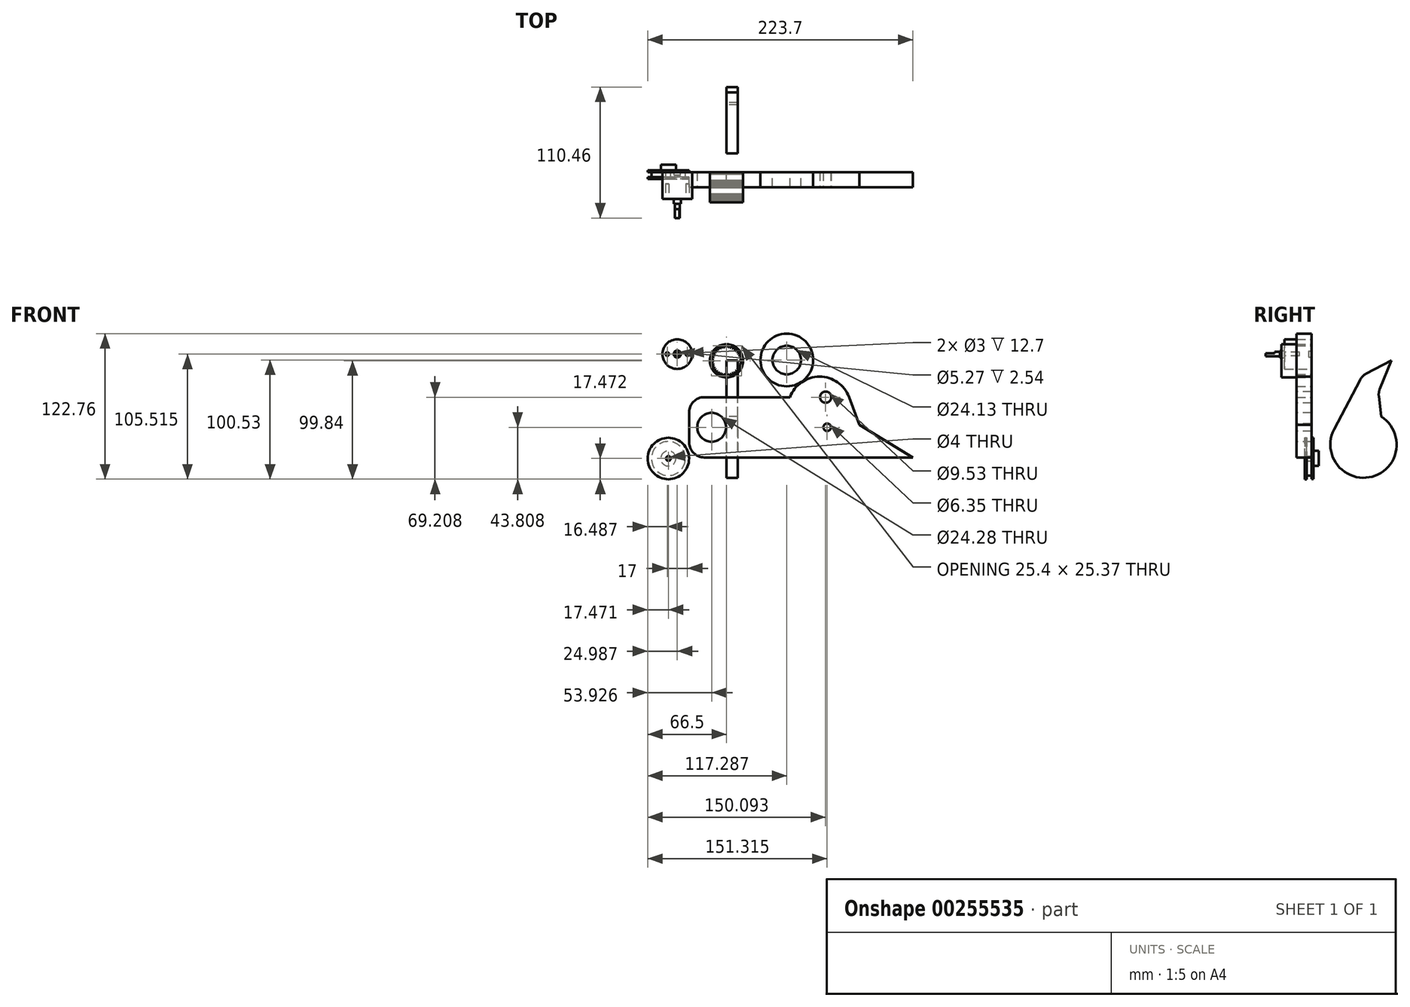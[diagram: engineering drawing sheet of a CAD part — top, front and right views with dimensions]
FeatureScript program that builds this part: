
annotation { "Feature Type Name" : "Feature", "Feature Type Description" : "" }
export const myFeature = defineFeature(function(context is Context, id is Id, definition is map)
    precondition{}
    {
        {
            var Q0;
            Q0=qCreatedBy(makeId("Front.planeOp"),FACE);
            var sketch = newSketch(context, id + "F0", { "sketchPlane" : qUnion([Q0])});
            skCircle(sketch, "E0", {"center": v(0, 41.16) * mm, "radius": 12.7 * mm});
            skLineSegment(sketch, "E1", {"start": v(-0.59, 28.47) * mm, "end": v(-0.26, 29.62) * mm});
            skLineSegment(sketch, "E2", {"start": v(-0.26, 29.62) * mm, "end": v(0, 29.62) * mm});
            skLineSegment(sketch, "E3", {"start": v(0, 28.46) * mm, "end": v(0, 28.58) * mm});
            skLineSegment(sketch, "E4.MirrorCS", {"start": v(0.59, 28.47) * mm, "end": v(0.26, 29.62) * mm});
            skLineSegment(sketch, "E5.MirrorCS", {"start": v(0.26, 29.62) * mm, "end": v(0, 29.62) * mm});
            skLineSegment(sketch, "E6.1.0", {"start": v(2.47, 28.7) * mm, "end": v(1.98, 29.78) * mm});
            skLineSegment(sketch, "E6.1.1", {"start": v(1.3, 28.53) * mm, "end": v(1.46, 29.7) * mm});
            skLineSegment(sketch, "E6.1.2", {"start": v(1.9, 28.6) * mm, "end": v(1.88, 28.72) * mm});
            skLineSegment(sketch, "E6.1.3", {"start": v(1.98, 29.78) * mm, "end": v(1.72, 29.75) * mm});
            skLineSegment(sketch, "E6.1.4", {"start": v(1.46, 29.7) * mm, "end": v(1.72, 29.75) * mm});
            skLineSegment(sketch, "E6.2.0", {"start": v(4.3, 29.21) * mm, "end": v(3.66, 30.2) * mm});
            skLineSegment(sketch, "E6.2.1", {"start": v(3.18, 28.86) * mm, "end": v(3.15, 30.05) * mm});
            skLineSegment(sketch, "E6.2.2", {"start": v(3.74, 29.02) * mm, "end": v(3.7, 29.13) * mm});
            skLineSegment(sketch, "E6.2.3", {"start": v(3.66, 30.2) * mm, "end": v(3.4, 30.13) * mm});
            skLineSegment(sketch, "E6.2.4", {"start": v(3.15, 30.05) * mm, "end": v(3.4, 30.13) * mm});
            skLineSegment(sketch, "E6.3.0", {"start": v(6.03, 29.99) * mm, "end": v(5.25, 30.87) * mm});
            skLineSegment(sketch, "E6.3.1", {"start": v(4.97, 29.48) * mm, "end": v(4.77, 30.64) * mm});
            skLineSegment(sketch, "E6.3.2", {"start": v(5.51, 29.72) * mm, "end": v(5.46, 29.82) * mm});
            skLineSegment(sketch, "E6.3.3", {"start": v(5.25, 30.87) * mm, "end": v(5, 30.76) * mm});
            skLineSegment(sketch, "E6.3.4", {"start": v(4.77, 30.64) * mm, "end": v(5, 30.76) * mm});
            skLineSegment(sketch, "E6.4.0", {"start": v(7.63, 31) * mm, "end": v(6.72, 31.77) * mm});
            skLineSegment(sketch, "E6.4.1", {"start": v(6.66, 30.35) * mm, "end": v(6.28, 31.47) * mm});
            skLineSegment(sketch, "E6.4.2", {"start": v(7.15, 30.67) * mm, "end": v(7.09, 30.76) * mm});
            skLineSegment(sketch, "E6.4.3", {"start": v(6.72, 31.77) * mm, "end": v(6.5, 31.62) * mm});
            skLineSegment(sketch, "E6.4.4", {"start": v(6.28, 31.47) * mm, "end": v(6.5, 31.62) * mm});
            skLineSegment(sketch, "E6.5.0", {"start": v(9.06, 32.26) * mm, "end": v(8.05, 32.88) * mm});
            skLineSegment(sketch, "E6.5.1", {"start": v(8.2, 31.46) * mm, "end": v(7.66, 32.52) * mm});
            skLineSegment(sketch, "E6.5.2", {"start": v(8.64, 31.85) * mm, "end": v(8.56, 31.93) * mm});
            skLineSegment(sketch, "E6.5.3", {"start": v(8.05, 32.88) * mm, "end": v(7.85, 32.7) * mm});
            skLineSegment(sketch, "E6.5.4", {"start": v(7.66, 32.52) * mm, "end": v(7.85, 32.7) * mm});
            skLineSegment(sketch, "E6.6.0", {"start": v(10.29, 33.71) * mm, "end": v(9.2, 34.17) * mm});
            skLineSegment(sketch, "E6.6.1", {"start": v(9.55, 32.8) * mm, "end": v(8.86, 33.76) * mm});
            skLineSegment(sketch, "E6.6.2", {"start": v(9.93, 33.24) * mm, "end": v(9.84, 33.31) * mm});
            skLineSegment(sketch, "E6.6.3", {"start": v(9.2, 34.17) * mm, "end": v(9.03, 33.96) * mm});
            skLineSegment(sketch, "E6.6.4", {"start": v(8.86, 33.76) * mm, "end": v(9.03, 33.96) * mm});
            skLineSegment(sketch, "E6.7.0", {"start": v(11.28, 35.33) * mm, "end": v(10.13, 35.62) * mm});
            skLineSegment(sketch, "E6.7.1", {"start": v(10.7, 34.3) * mm, "end": v(9.87, 35.16) * mm});
            skLineSegment(sketch, "E6.7.2", {"start": v(11, 34.81) * mm, "end": v(10.9, 34.87) * mm});
            skLineSegment(sketch, "E6.7.3", {"start": v(10.13, 35.62) * mm, "end": v(10, 35.39) * mm});
            skLineSegment(sketch, "E6.7.4", {"start": v(9.87, 35.16) * mm, "end": v(10, 35.39) * mm});
            skLineSegment(sketch, "E6.8.0", {"start": v(12.02, 37.07) * mm, "end": v(10.84, 37.19) * mm});
            skLineSegment(sketch, "E6.8.1", {"start": v(11.6, 35.98) * mm, "end": v(10.65, 36.7) * mm});
            skLineSegment(sketch, "E6.8.2", {"start": v(11.82, 36.52) * mm, "end": v(11.72, 36.56) * mm});
            skLineSegment(sketch, "E6.8.3", {"start": v(10.84, 37.19) * mm, "end": v(10.75, 36.94) * mm});
            skLineSegment(sketch, "E6.8.4", {"start": v(10.65, 36.7) * mm, "end": v(10.75, 36.94) * mm});
            skLineSegment(sketch, "E6.9.0", {"start": v(12.5, 38.91) * mm, "end": v(11.31, 38.85) * mm});
            skLineSegment(sketch, "E6.9.1", {"start": v(12.24, 37.76) * mm, "end": v(11.2, 38.33) * mm});
            skLineSegment(sketch, "E6.9.2", {"start": v(12.38, 38.33) * mm, "end": v(12.27, 38.36) * mm});
            skLineSegment(sketch, "E6.9.3", {"start": v(11.31, 38.85) * mm, "end": v(11.25, 38.6) * mm});
            skLineSegment(sketch, "E6.9.4", {"start": v(11.2, 38.33) * mm, "end": v(11.25, 38.6) * mm});
            skLineSegment(sketch, "E6.10.0", {"start": v(12.7, 40.8) * mm, "end": v(11.53, 40.56) * mm});
            skLineSegment(sketch, "E6.10.1", {"start": v(12.6, 39.63) * mm, "end": v(11.5, 40.03) * mm});
            skLineSegment(sketch, "E6.10.2", {"start": v(12.66, 40.21) * mm, "end": v(12.55, 40.22) * mm});
            skLineSegment(sketch, "E6.10.3", {"start": v(11.53, 40.56) * mm, "end": v(11.51, 40.3) * mm});
            skLineSegment(sketch, "E6.10.4", {"start": v(11.5, 40.03) * mm, "end": v(11.51, 40.3) * mm});
            skLineSegment(sketch, "E6.11.0", {"start": v(12.6, 42.7) * mm, "end": v(11.5, 42.29) * mm});
            skLineSegment(sketch, "E6.11.1", {"start": v(12.7, 41.52) * mm, "end": v(11.53, 41.76) * mm});
            skLineSegment(sketch, "E6.11.2", {"start": v(12.66, 42.1) * mm, "end": v(12.55, 42.1) * mm});
            skLineSegment(sketch, "E6.11.3", {"start": v(11.5, 42.29) * mm, "end": v(11.51, 42.02) * mm});
            skLineSegment(sketch, "E6.11.4", {"start": v(11.53, 41.76) * mm, "end": v(11.51, 42.02) * mm});
            skLineSegment(sketch, "E6.12.0", {"start": v(12.24, 44.56) * mm, "end": v(11.2, 43.99) * mm});
            skLineSegment(sketch, "E6.12.1", {"start": v(12.5, 43.41) * mm, "end": v(11.31, 43.47) * mm});
            skLineSegment(sketch, "E6.12.2", {"start": v(12.38, 43.99) * mm, "end": v(12.27, 43.96) * mm});
            skLineSegment(sketch, "E6.12.3", {"start": v(11.2, 43.99) * mm, "end": v(11.25, 43.73) * mm});
            skLineSegment(sketch, "E6.12.4", {"start": v(11.31, 43.47) * mm, "end": v(11.25, 43.73) * mm});
            skLineSegment(sketch, "E6.13.0", {"start": v(11.6, 46.34) * mm, "end": v(10.65, 45.62) * mm});
            skLineSegment(sketch, "E6.13.1", {"start": v(12.02, 45.25) * mm, "end": v(10.84, 45.13) * mm});
            skLineSegment(sketch, "E6.13.2", {"start": v(11.82, 45.8) * mm, "end": v(11.72, 45.76) * mm});
            skLineSegment(sketch, "E6.13.3", {"start": v(10.65, 45.62) * mm, "end": v(10.75, 45.38) * mm});
            skLineSegment(sketch, "E6.13.4", {"start": v(10.84, 45.13) * mm, "end": v(10.75, 45.38) * mm});
            skLineSegment(sketch, "E6.14.0", {"start": v(10.7, 48.01) * mm, "end": v(9.87, 47.16) * mm});
            skLineSegment(sketch, "E6.14.1", {"start": v(11.28, 47) * mm, "end": v(10.13, 46.7) * mm});
            skLineSegment(sketch, "E6.14.2", {"start": v(11, 47.51) * mm, "end": v(10.9, 47.45) * mm});
            skLineSegment(sketch, "E6.14.3", {"start": v(9.87, 47.16) * mm, "end": v(10, 46.93) * mm});
            skLineSegment(sketch, "E6.14.4", {"start": v(10.13, 46.7) * mm, "end": v(10, 46.93) * mm});
            skLineSegment(sketch, "E6.15.0", {"start": v(9.55, 49.53) * mm, "end": v(8.86, 48.56) * mm});
            skLineSegment(sketch, "E6.15.1", {"start": v(10.29, 48.61) * mm, "end": v(9.2, 48.15) * mm});
            skLineSegment(sketch, "E6.15.2", {"start": v(9.93, 49.08) * mm, "end": v(9.84, 49) * mm});
            skLineSegment(sketch, "E6.15.3", {"start": v(8.86, 48.56) * mm, "end": v(9.03, 48.36) * mm});
            skLineSegment(sketch, "E6.15.4", {"start": v(9.2, 48.15) * mm, "end": v(9.03, 48.36) * mm});
            skLineSegment(sketch, "E6.16.0", {"start": v(8.2, 50.86) * mm, "end": v(7.66, 49.8) * mm});
            skLineSegment(sketch, "E6.16.1", {"start": v(9.06, 50.06) * mm, "end": v(8.05, 49.44) * mm});
            skLineSegment(sketch, "E6.16.2", {"start": v(8.64, 50.47) * mm, "end": v(8.56, 50.39) * mm});
            skLineSegment(sketch, "E6.16.3", {"start": v(7.66, 49.8) * mm, "end": v(7.85, 49.62) * mm});
            skLineSegment(sketch, "E6.16.4", {"start": v(8.05, 49.44) * mm, "end": v(7.85, 49.62) * mm});
            skLineSegment(sketch, "E6.17.0", {"start": v(6.66, 51.97) * mm, "end": v(6.28, 50.85) * mm});
            skLineSegment(sketch, "E6.17.1", {"start": v(7.63, 51.31) * mm, "end": v(6.72, 50.55) * mm});
            skLineSegment(sketch, "E6.17.2", {"start": v(7.15, 51.65) * mm, "end": v(7.09, 51.56) * mm});
            skLineSegment(sketch, "E6.17.3", {"start": v(6.28, 50.85) * mm, "end": v(6.5, 50.7) * mm});
            skLineSegment(sketch, "E6.17.4", {"start": v(6.72, 50.55) * mm, "end": v(6.5, 50.7) * mm});
            skLineSegment(sketch, "E6.18.0", {"start": v(4.97, 52.85) * mm, "end": v(4.77, 51.68) * mm});
            skLineSegment(sketch, "E6.18.1", {"start": v(6.03, 52.34) * mm, "end": v(5.25, 51.45) * mm});
            skLineSegment(sketch, "E6.18.2", {"start": v(5.51, 52.6) * mm, "end": v(5.46, 52.5) * mm});
            skLineSegment(sketch, "E6.18.3", {"start": v(4.77, 51.68) * mm, "end": v(5, 51.56) * mm});
            skLineSegment(sketch, "E6.18.4", {"start": v(5.25, 51.45) * mm, "end": v(5, 51.56) * mm});
            skLineSegment(sketch, "E6.19.0", {"start": v(3.18, 53.46) * mm, "end": v(3.15, 52.27) * mm});
            skLineSegment(sketch, "E6.19.1", {"start": v(4.3, 53.1) * mm, "end": v(3.66, 52.11) * mm});
            skLineSegment(sketch, "E6.19.2", {"start": v(3.74, 53.3) * mm, "end": v(3.7, 53.19) * mm});
            skLineSegment(sketch, "E6.19.3", {"start": v(3.15, 52.27) * mm, "end": v(3.4, 52.2) * mm});
            skLineSegment(sketch, "E6.19.4", {"start": v(3.66, 52.11) * mm, "end": v(3.4, 52.2) * mm});
            skLineSegment(sketch, "E6.20.0", {"start": v(1.3, 53.8) * mm, "end": v(1.46, 52.62) * mm});
            skLineSegment(sketch, "E6.20.1", {"start": v(2.47, 53.62) * mm, "end": v(1.98, 52.54) * mm});
            skLineSegment(sketch, "E6.20.2", {"start": v(1.9, 53.72) * mm, "end": v(1.88, 53.6) * mm});
            skLineSegment(sketch, "E6.20.3", {"start": v(1.46, 52.62) * mm, "end": v(1.72, 52.58) * mm});
            skLineSegment(sketch, "E6.20.4", {"start": v(1.98, 52.54) * mm, "end": v(1.72, 52.58) * mm});
            skLineSegment(sketch, "E6.21.0", {"start": v(-0.59, 53.85) * mm, "end": v(-0.26, 52.7) * mm});
            skLineSegment(sketch, "E6.21.1", {"start": v(0.59, 53.85) * mm, "end": v(0.26, 52.7) * mm});
            skLineSegment(sketch, "E6.21.2", {"start": v(0, 53.86) * mm, "end": v(0, 53.75) * mm});
            skLineSegment(sketch, "E6.21.3", {"start": v(-0.26, 52.7) * mm, "end": v(0, 52.7) * mm});
            skLineSegment(sketch, "E6.21.4", {"start": v(0.26, 52.7) * mm, "end": v(0, 52.7) * mm});
            skLineSegment(sketch, "E6.22.0", {"start": v(-2.47, 53.62) * mm, "end": v(-1.98, 52.54) * mm});
            skLineSegment(sketch, "E6.22.1", {"start": v(-1.3, 53.8) * mm, "end": v(-1.46, 52.62) * mm});
            skLineSegment(sketch, "E6.22.2", {"start": v(-1.9, 53.72) * mm, "end": v(-1.88, 53.6) * mm});
            skLineSegment(sketch, "E6.22.3", {"start": v(-1.98, 52.54) * mm, "end": v(-1.72, 52.58) * mm});
            skLineSegment(sketch, "E6.22.4", {"start": v(-1.46, 52.62) * mm, "end": v(-1.72, 52.58) * mm});
            skLineSegment(sketch, "E6.23.0", {"start": v(-4.3, 53.1) * mm, "end": v(-3.66, 52.11) * mm});
            skLineSegment(sketch, "E6.23.1", {"start": v(-3.18, 53.46) * mm, "end": v(-3.15, 52.27) * mm});
            skLineSegment(sketch, "E6.23.2", {"start": v(-3.74, 53.3) * mm, "end": v(-3.7, 53.19) * mm});
            skLineSegment(sketch, "E6.23.3", {"start": v(-3.66, 52.11) * mm, "end": v(-3.4, 52.2) * mm});
            skLineSegment(sketch, "E6.23.4", {"start": v(-3.15, 52.27) * mm, "end": v(-3.4, 52.2) * mm});
            skLineSegment(sketch, "E6.24.0", {"start": v(-6.03, 52.34) * mm, "end": v(-5.25, 51.45) * mm});
            skLineSegment(sketch, "E6.24.1", {"start": v(-4.97, 52.85) * mm, "end": v(-4.77, 51.68) * mm});
            skLineSegment(sketch, "E6.24.2", {"start": v(-5.51, 52.6) * mm, "end": v(-5.46, 52.5) * mm});
            skLineSegment(sketch, "E6.24.3", {"start": v(-5.25, 51.45) * mm, "end": v(-5, 51.56) * mm});
            skLineSegment(sketch, "E6.24.4", {"start": v(-4.77, 51.68) * mm, "end": v(-5, 51.56) * mm});
            skLineSegment(sketch, "E6.25.0", {"start": v(-7.63, 51.31) * mm, "end": v(-6.72, 50.55) * mm});
            skLineSegment(sketch, "E6.25.1", {"start": v(-6.66, 51.97) * mm, "end": v(-6.28, 50.85) * mm});
            skLineSegment(sketch, "E6.25.2", {"start": v(-7.15, 51.65) * mm, "end": v(-7.09, 51.56) * mm});
            skLineSegment(sketch, "E6.25.3", {"start": v(-6.72, 50.55) * mm, "end": v(-6.5, 50.7) * mm});
            skLineSegment(sketch, "E6.25.4", {"start": v(-6.28, 50.85) * mm, "end": v(-6.5, 50.7) * mm});
            skLineSegment(sketch, "E6.26.0", {"start": v(-9.06, 50.06) * mm, "end": v(-8.05, 49.44) * mm});
            skLineSegment(sketch, "E6.26.1", {"start": v(-8.2, 50.86) * mm, "end": v(-7.66, 49.8) * mm});
            skLineSegment(sketch, "E6.26.2", {"start": v(-8.64, 50.47) * mm, "end": v(-8.56, 50.39) * mm});
            skLineSegment(sketch, "E6.26.3", {"start": v(-8.05, 49.44) * mm, "end": v(-7.85, 49.62) * mm});
            skLineSegment(sketch, "E6.26.4", {"start": v(-7.66, 49.8) * mm, "end": v(-7.85, 49.62) * mm});
            skLineSegment(sketch, "E6.27.0", {"start": v(-10.29, 48.61) * mm, "end": v(-9.2, 48.15) * mm});
            skLineSegment(sketch, "E6.27.1", {"start": v(-9.55, 49.53) * mm, "end": v(-8.86, 48.56) * mm});
            skLineSegment(sketch, "E6.27.2", {"start": v(-9.93, 49.08) * mm, "end": v(-9.84, 49) * mm});
            skLineSegment(sketch, "E6.27.3", {"start": v(-9.2, 48.15) * mm, "end": v(-9.03, 48.36) * mm});
            skLineSegment(sketch, "E6.27.4", {"start": v(-8.86, 48.56) * mm, "end": v(-9.03, 48.36) * mm});
            skLineSegment(sketch, "E6.28.0", {"start": v(-11.28, 47) * mm, "end": v(-10.13, 46.7) * mm});
            skLineSegment(sketch, "E6.28.1", {"start": v(-10.7, 48.01) * mm, "end": v(-9.87, 47.16) * mm});
            skLineSegment(sketch, "E6.28.2", {"start": v(-11, 47.51) * mm, "end": v(-10.9, 47.45) * mm});
            skLineSegment(sketch, "E6.28.3", {"start": v(-10.13, 46.7) * mm, "end": v(-10, 46.93) * mm});
            skLineSegment(sketch, "E6.28.4", {"start": v(-9.87, 47.16) * mm, "end": v(-10, 46.93) * mm});
            skLineSegment(sketch, "E6.29.0", {"start": v(-12.02, 45.25) * mm, "end": v(-10.84, 45.13) * mm});
            skLineSegment(sketch, "E6.29.1", {"start": v(-11.6, 46.34) * mm, "end": v(-10.65, 45.62) * mm});
            skLineSegment(sketch, "E6.29.2", {"start": v(-11.82, 45.8) * mm, "end": v(-11.72, 45.76) * mm});
            skLineSegment(sketch, "E6.29.3", {"start": v(-10.84, 45.13) * mm, "end": v(-10.75, 45.38) * mm});
            skLineSegment(sketch, "E6.29.4", {"start": v(-10.65, 45.62) * mm, "end": v(-10.75, 45.38) * mm});
            skLineSegment(sketch, "E6.30.0", {"start": v(-12.5, 43.41) * mm, "end": v(-11.31, 43.47) * mm});
            skLineSegment(sketch, "E6.30.1", {"start": v(-12.24, 44.56) * mm, "end": v(-11.2, 43.99) * mm});
            skLineSegment(sketch, "E6.30.2", {"start": v(-12.38, 43.99) * mm, "end": v(-12.27, 43.96) * mm});
            skLineSegment(sketch, "E6.30.3", {"start": v(-11.31, 43.47) * mm, "end": v(-11.25, 43.73) * mm});
            skLineSegment(sketch, "E6.30.4", {"start": v(-11.2, 43.99) * mm, "end": v(-11.25, 43.73) * mm});
            skLineSegment(sketch, "E6.31.0", {"start": v(-12.7, 41.52) * mm, "end": v(-11.53, 41.76) * mm});
            skLineSegment(sketch, "E6.31.1", {"start": v(-12.6, 42.7) * mm, "end": v(-11.5, 42.29) * mm});
            skLineSegment(sketch, "E6.31.2", {"start": v(-12.66, 42.1) * mm, "end": v(-12.55, 42.1) * mm});
            skLineSegment(sketch, "E6.31.3", {"start": v(-11.53, 41.76) * mm, "end": v(-11.51, 42.02) * mm});
            skLineSegment(sketch, "E6.31.4", {"start": v(-11.5, 42.29) * mm, "end": v(-11.51, 42.02) * mm});
            skLineSegment(sketch, "E6.32.0", {"start": v(-12.6, 39.63) * mm, "end": v(-11.5, 40.03) * mm});
            skLineSegment(sketch, "E6.32.1", {"start": v(-12.7, 40.8) * mm, "end": v(-11.53, 40.56) * mm});
            skLineSegment(sketch, "E6.32.2", {"start": v(-12.66, 40.21) * mm, "end": v(-12.55, 40.22) * mm});
            skLineSegment(sketch, "E6.32.3", {"start": v(-11.5, 40.03) * mm, "end": v(-11.51, 40.3) * mm});
            skLineSegment(sketch, "E6.32.4", {"start": v(-11.53, 40.56) * mm, "end": v(-11.51, 40.3) * mm});
            skLineSegment(sketch, "E6.33.0", {"start": v(-12.24, 37.76) * mm, "end": v(-11.2, 38.33) * mm});
            skLineSegment(sketch, "E6.33.1", {"start": v(-12.5, 38.91) * mm, "end": v(-11.31, 38.85) * mm});
            skLineSegment(sketch, "E6.33.2", {"start": v(-12.38, 38.33) * mm, "end": v(-12.27, 38.36) * mm});
            skLineSegment(sketch, "E6.33.3", {"start": v(-11.2, 38.33) * mm, "end": v(-11.25, 38.6) * mm});
            skLineSegment(sketch, "E6.33.4", {"start": v(-11.31, 38.85) * mm, "end": v(-11.25, 38.6) * mm});
            skLineSegment(sketch, "E6.34.0", {"start": v(-11.6, 35.98) * mm, "end": v(-10.65, 36.7) * mm});
            skLineSegment(sketch, "E6.34.1", {"start": v(-12.02, 37.07) * mm, "end": v(-10.84, 37.19) * mm});
            skLineSegment(sketch, "E6.34.2", {"start": v(-11.82, 36.52) * mm, "end": v(-11.72, 36.56) * mm});
            skLineSegment(sketch, "E6.34.3", {"start": v(-10.65, 36.7) * mm, "end": v(-10.75, 36.94) * mm});
            skLineSegment(sketch, "E6.34.4", {"start": v(-10.84, 37.19) * mm, "end": v(-10.75, 36.94) * mm});
            skLineSegment(sketch, "E6.35.0", {"start": v(-10.7, 34.3) * mm, "end": v(-9.87, 35.16) * mm});
            skLineSegment(sketch, "E6.35.1", {"start": v(-11.28, 35.33) * mm, "end": v(-10.13, 35.62) * mm});
            skLineSegment(sketch, "E6.35.2", {"start": v(-11, 34.81) * mm, "end": v(-10.9, 34.87) * mm});
            skLineSegment(sketch, "E6.35.3", {"start": v(-9.87, 35.16) * mm, "end": v(-10, 35.39) * mm});
            skLineSegment(sketch, "E6.35.4", {"start": v(-10.13, 35.62) * mm, "end": v(-10, 35.39) * mm});
            skLineSegment(sketch, "E6.36.0", {"start": v(-9.55, 32.8) * mm, "end": v(-8.86, 33.76) * mm});
            skLineSegment(sketch, "E6.36.1", {"start": v(-10.29, 33.71) * mm, "end": v(-9.2, 34.17) * mm});
            skLineSegment(sketch, "E6.36.2", {"start": v(-9.93, 33.24) * mm, "end": v(-9.84, 33.31) * mm});
            skLineSegment(sketch, "E6.36.3", {"start": v(-8.86, 33.76) * mm, "end": v(-9.03, 33.96) * mm});
            skLineSegment(sketch, "E6.36.4", {"start": v(-9.2, 34.17) * mm, "end": v(-9.03, 33.96) * mm});
            skLineSegment(sketch, "E6.37.0", {"start": v(-8.2, 31.46) * mm, "end": v(-7.66, 32.52) * mm});
            skLineSegment(sketch, "E6.37.1", {"start": v(-9.06, 32.26) * mm, "end": v(-8.05, 32.88) * mm});
            skLineSegment(sketch, "E6.37.2", {"start": v(-8.64, 31.85) * mm, "end": v(-8.56, 31.93) * mm});
            skLineSegment(sketch, "E6.37.3", {"start": v(-7.66, 32.52) * mm, "end": v(-7.85, 32.7) * mm});
            skLineSegment(sketch, "E6.37.4", {"start": v(-8.05, 32.88) * mm, "end": v(-7.85, 32.7) * mm});
            skLineSegment(sketch, "E6.38.0", {"start": v(-6.66, 30.35) * mm, "end": v(-6.28, 31.47) * mm});
            skLineSegment(sketch, "E6.38.1", {"start": v(-7.63, 31) * mm, "end": v(-6.72, 31.77) * mm});
            skLineSegment(sketch, "E6.38.2", {"start": v(-7.15, 30.67) * mm, "end": v(-7.09, 30.76) * mm});
            skLineSegment(sketch, "E6.38.3", {"start": v(-6.28, 31.47) * mm, "end": v(-6.5, 31.62) * mm});
            skLineSegment(sketch, "E6.38.4", {"start": v(-6.72, 31.77) * mm, "end": v(-6.5, 31.62) * mm});
            skLineSegment(sketch, "E6.39.0", {"start": v(-4.97, 29.48) * mm, "end": v(-4.77, 30.64) * mm});
            skLineSegment(sketch, "E6.39.1", {"start": v(-6.03, 29.99) * mm, "end": v(-5.25, 30.87) * mm});
            skLineSegment(sketch, "E6.39.2", {"start": v(-5.51, 29.72) * mm, "end": v(-5.46, 29.82) * mm});
            skLineSegment(sketch, "E6.39.3", {"start": v(-4.77, 30.64) * mm, "end": v(-5, 30.76) * mm});
            skLineSegment(sketch, "E6.39.4", {"start": v(-5.25, 30.87) * mm, "end": v(-5, 30.76) * mm});
            skLineSegment(sketch, "E6.40.0", {"start": v(-3.18, 28.86) * mm, "end": v(-3.15, 30.05) * mm});
            skLineSegment(sketch, "E6.40.1", {"start": v(-4.3, 29.21) * mm, "end": v(-3.66, 30.2) * mm});
            skLineSegment(sketch, "E6.40.2", {"start": v(-3.74, 29.02) * mm, "end": v(-3.7, 29.13) * mm});
            skLineSegment(sketch, "E6.40.3", {"start": v(-3.15, 30.05) * mm, "end": v(-3.4, 30.13) * mm});
            skLineSegment(sketch, "E6.40.4", {"start": v(-3.66, 30.2) * mm, "end": v(-3.4, 30.13) * mm});
            skLineSegment(sketch, "E6.41.0", {"start": v(-1.3, 28.53) * mm, "end": v(-1.46, 29.7) * mm});
            skLineSegment(sketch, "E6.41.1", {"start": v(-2.47, 28.7) * mm, "end": v(-1.98, 29.78) * mm});
            skLineSegment(sketch, "E6.41.2", {"start": v(-1.9, 28.6) * mm, "end": v(-1.88, 28.72) * mm});
            skLineSegment(sketch, "E6.41.3", {"start": v(-1.46, 29.7) * mm, "end": v(-1.72, 29.75) * mm});
            skLineSegment(sketch, "E6.41.4", {"start": v(-1.98, 29.78) * mm, "end": v(-1.72, 29.75) * mm});
            skCircle(sketch, "E7", {"center": v(0, 41.16) * mm, "radius": 13.98 * mm});
            skSolve(sketch);
        }
        {
            var Q0;
            Q0 = qSketchRegion(id + "F0", true);
            var Q1;
            {var subQ1=sQuery(id+"F0.wireOp",EDGE,"E6.25.0");Q1=makeQuery(id+"F0.imprint","IMPRINT",FACE,{"disambiguationData":[TD([[makeQuery(id+"F0.imprint","IMPRINT",EDGE,{"derivedFrom":subQ1}),1.0]])]});}
            var Q2;
            {var subQ3=sQuery(id+"F0.wireOp",EDGE,"E6.26.0");Q2=makeQuery(id+"F0.imprint","IMPRINT",FACE,{"disambiguationData":[TD([[makeQuery(id+"F0.imprint","IMPRINT",EDGE,{"derivedFrom":subQ3}),1.0]])]});}
            var Q3;
            {var subQ1=sQuery(id+"F0.wireOp",EDGE,"E6.27.0");Q3=makeQuery(id+"F0.imprint","IMPRINT",FACE,{"disambiguationData":[TD([[makeQuery(id+"F0.imprint","IMPRINT",EDGE,{"derivedFrom":subQ1}),1.0]])]});}
            var Q4;
            {var subQ1=sQuery(id+"F0.wireOp",EDGE,"E6.28.0");Q4=makeQuery(id+"F0.imprint","IMPRINT",FACE,{"disambiguationData":[TD([[makeQuery(id+"F0.imprint","IMPRINT",EDGE,{"derivedFrom":subQ1}),1.0]])]});}
            var Q5;
            {var subQ1=sQuery(id+"F0.wireOp",EDGE,"E6.29.0");Q5=makeQuery(id+"F0.imprint","IMPRINT",FACE,{"disambiguationData":[TD([[makeQuery(id+"F0.imprint","IMPRINT",EDGE,{"derivedFrom":subQ1}),1.0]])]});}
            var Q6;
            {var subQ1=sQuery(id+"F0.wireOp",EDGE,"E6.30.0");Q6=makeQuery(id+"F0.imprint","IMPRINT",FACE,{"disambiguationData":[TD([[makeQuery(id+"F0.imprint","IMPRINT",EDGE,{"derivedFrom":subQ1}),1.0]])]});}
            var Q7;
            {var subQ1=sQuery(id+"F0.wireOp",EDGE,"E6.31.0");Q7=makeQuery(id+"F0.imprint","IMPRINT",FACE,{"disambiguationData":[TD([[makeQuery(id+"F0.imprint","IMPRINT",EDGE,{"derivedFrom":subQ1}),1.0]])]});}
            var Q8;
            {var subQ1=sQuery(id+"F0.wireOp",EDGE,"E6.32.0");Q8=makeQuery(id+"F0.imprint","IMPRINT",FACE,{"disambiguationData":[TD([[makeQuery(id+"F0.imprint","IMPRINT",EDGE,{"derivedFrom":subQ1}),1.0]])]});}
            var Q9;
            {var subQ1=sQuery(id+"F0.wireOp",EDGE,"E6.33.0");Q9=makeQuery(id+"F0.imprint","IMPRINT",FACE,{"disambiguationData":[TD([[makeQuery(id+"F0.imprint","IMPRINT",EDGE,{"derivedFrom":subQ1}),1.0]])]});}
            var Q10;
            {var subQ1=sQuery(id+"F0.wireOp",EDGE,"E6.34.0");Q10=makeQuery(id+"F0.imprint","IMPRINT",FACE,{"disambiguationData":[TD([[makeQuery(id+"F0.imprint","IMPRINT",EDGE,{"derivedFrom":subQ1}),1.0]])]});}
            var Q11;
            {var subQ1=sQuery(id+"F0.wireOp",EDGE,"E6.35.0");Q11=makeQuery(id+"F0.imprint","IMPRINT",FACE,{"disambiguationData":[TD([[makeQuery(id+"F0.imprint","IMPRINT",EDGE,{"derivedFrom":subQ1}),1.0]])]});}
            var Q12;
            {var subQ1=sQuery(id+"F0.wireOp",EDGE,"E6.36.0");Q12=makeQuery(id+"F0.imprint","IMPRINT",FACE,{"disambiguationData":[TD([[makeQuery(id+"F0.imprint","IMPRINT",EDGE,{"derivedFrom":subQ1}),1.0]])]});}
            var Q13;
            {var subQ1=sQuery(id+"F0.wireOp",EDGE,"E6.37.0");Q13=makeQuery(id+"F0.imprint","IMPRINT",FACE,{"disambiguationData":[TD([[makeQuery(id+"F0.imprint","IMPRINT",EDGE,{"derivedFrom":subQ1}),1.0]])]});}
            var Q14;
            {var subQ1=sQuery(id+"F0.wireOp",EDGE,"E6.38.0");Q14=makeQuery(id+"F0.imprint","IMPRINT",FACE,{"disambiguationData":[TD([[makeQuery(id+"F0.imprint","IMPRINT",EDGE,{"derivedFrom":subQ1}),1.0]])]});}
            var Q15;
            {var subQ3=sQuery(id+"F0.wireOp",EDGE,"E6.39.0");Q15=makeQuery(id+"F0.imprint","IMPRINT",FACE,{"disambiguationData":[TD([[makeQuery(id+"F0.imprint","IMPRINT",EDGE,{"derivedFrom":subQ3}),1.0]])]});}
            var Q16;
            {var subQ0=sQuery(id+"F0.wireOp",EDGE,"E6.40.0");Q16=makeQuery(id+"F0.imprint","IMPRINT",FACE,{"disambiguationData":[TD([[makeQuery(id+"F0.imprint","IMPRINT",EDGE,{"derivedFrom":subQ0}),1.0]])]});}
            var Q17;
            {var subQ1=sQuery(id+"F0.wireOp",EDGE,"E6.41.0");Q17=makeQuery(id+"F0.imprint","IMPRINT",FACE,{"disambiguationData":[TD([[makeQuery(id+"F0.imprint","IMPRINT",EDGE,{"derivedFrom":subQ1}),1.0]])]});}
            var Q18;
            {var subQ0=sQuery(id+"F0.wireOp",EDGE,"E1");Q18=makeQuery(id+"F0.imprint","IMPRINT",FACE,{"disambiguationData":[TD([[makeQuery(id+"F0.imprint","IMPRINT",EDGE,{"derivedFrom":subQ0}),-1.0]])]});}
            var Q19;
            {var subQ1=sQuery(id+"F0.wireOp",EDGE,"E6.1.0");Q19=makeQuery(id+"F0.imprint","IMPRINT",FACE,{"disambiguationData":[TD([[makeQuery(id+"F0.imprint","IMPRINT",EDGE,{"derivedFrom":subQ1}),1.0]])]});}
            var Q20;
            {var subQ1=sQuery(id+"F0.wireOp",EDGE,"E6.2.0");Q20=makeQuery(id+"F0.imprint","IMPRINT",FACE,{"disambiguationData":[TD([[makeQuery(id+"F0.imprint","IMPRINT",EDGE,{"derivedFrom":subQ1}),1.0]])]});}
            var Q21;
            {var subQ1=sQuery(id+"F0.wireOp",EDGE,"E6.3.0");Q21=makeQuery(id+"F0.imprint","IMPRINT",FACE,{"disambiguationData":[TD([[makeQuery(id+"F0.imprint","IMPRINT",EDGE,{"derivedFrom":subQ1}),1.0]])]});}
            var Q22;
            {var subQ3=sQuery(id+"F0.wireOp",EDGE,"E6.4.0");Q22=makeQuery(id+"F0.imprint","IMPRINT",FACE,{"disambiguationData":[TD([[makeQuery(id+"F0.imprint","IMPRINT",EDGE,{"derivedFrom":subQ3}),1.0]])]});}
            var Q23;
            {var subQ1=sQuery(id+"F0.wireOp",EDGE,"E6.6.0");Q23=makeQuery(id+"F0.imprint","IMPRINT",FACE,{"disambiguationData":[TD([[makeQuery(id+"F0.imprint","IMPRINT",EDGE,{"derivedFrom":subQ1}),1.0]])]});}
            var Q24;
            {var subQ1=sQuery(id+"F0.wireOp",EDGE,"E6.7.0");Q24=makeQuery(id+"F0.imprint","IMPRINT",FACE,{"disambiguationData":[TD([[makeQuery(id+"F0.imprint","IMPRINT",EDGE,{"derivedFrom":subQ1}),1.0]])]});}
            var Q25;
            {var subQ1=sQuery(id+"F0.wireOp",EDGE,"E6.8.0");Q25=makeQuery(id+"F0.imprint","IMPRINT",FACE,{"disambiguationData":[TD([[makeQuery(id+"F0.imprint","IMPRINT",EDGE,{"derivedFrom":subQ1}),1.0]])]});}
            var Q26;
            {var subQ1=sQuery(id+"F0.wireOp",EDGE,"E6.9.0");Q26=makeQuery(id+"F0.imprint","IMPRINT",FACE,{"disambiguationData":[TD([[makeQuery(id+"F0.imprint","IMPRINT",EDGE,{"derivedFrom":subQ1}),1.0]])]});}
            var Q27;
            {var subQ1=sQuery(id+"F0.wireOp",EDGE,"E6.5.0");Q27=makeQuery(id+"F0.imprint","IMPRINT",FACE,{"disambiguationData":[TD([[makeQuery(id+"F0.imprint","IMPRINT",EDGE,{"derivedFrom":subQ1}),1.0]])]});}
            var Q28;
            {var subQ1=sQuery(id+"F0.wireOp",EDGE,"E6.10.0");Q28=makeQuery(id+"F0.imprint","IMPRINT",FACE,{"disambiguationData":[TD([[makeQuery(id+"F0.imprint","IMPRINT",EDGE,{"derivedFrom":subQ1}),1.0]])]});}
            var Q29;
            {var subQ1=sQuery(id+"F0.wireOp",EDGE,"E6.11.0");Q29=makeQuery(id+"F0.imprint","IMPRINT",FACE,{"disambiguationData":[TD([[makeQuery(id+"F0.imprint","IMPRINT",EDGE,{"derivedFrom":subQ1}),1.0]])]});}
            var Q30;
            {var subQ1=sQuery(id+"F0.wireOp",EDGE,"E6.12.0");Q30=makeQuery(id+"F0.imprint","IMPRINT",FACE,{"disambiguationData":[TD([[makeQuery(id+"F0.imprint","IMPRINT",EDGE,{"derivedFrom":subQ1}),1.0]])]});}
            var Q31;
            {var subQ1=sQuery(id+"F0.wireOp",EDGE,"E6.13.0");Q31=makeQuery(id+"F0.imprint","IMPRINT",FACE,{"disambiguationData":[TD([[makeQuery(id+"F0.imprint","IMPRINT",EDGE,{"derivedFrom":subQ1}),1.0]])]});}
            var Q32;
            {var subQ1=sQuery(id+"F0.wireOp",EDGE,"E6.14.0");Q32=makeQuery(id+"F0.imprint","IMPRINT",FACE,{"disambiguationData":[TD([[makeQuery(id+"F0.imprint","IMPRINT",EDGE,{"derivedFrom":subQ1}),1.0]])]});}
            var Q33;
            {var subQ1=sQuery(id+"F0.wireOp",EDGE,"E6.15.0");Q33=makeQuery(id+"F0.imprint","IMPRINT",FACE,{"disambiguationData":[TD([[makeQuery(id+"F0.imprint","IMPRINT",EDGE,{"derivedFrom":subQ1}),1.0]])]});}
            var Q34;
            {var subQ1=sQuery(id+"F0.wireOp",EDGE,"E6.16.0");Q34=makeQuery(id+"F0.imprint","IMPRINT",FACE,{"disambiguationData":[TD([[makeQuery(id+"F0.imprint","IMPRINT",EDGE,{"derivedFrom":subQ1}),1.0]])]});}
            var Q35;
            {var subQ1=sQuery(id+"F0.wireOp",EDGE,"E6.17.0");Q35=makeQuery(id+"F0.imprint","IMPRINT",FACE,{"disambiguationData":[TD([[makeQuery(id+"F0.imprint","IMPRINT",EDGE,{"derivedFrom":subQ1}),1.0]])]});}
            var Q36;
            {var subQ1=sQuery(id+"F0.wireOp",EDGE,"E6.18.0");Q36=makeQuery(id+"F0.imprint","IMPRINT",FACE,{"disambiguationData":[TD([[makeQuery(id+"F0.imprint","IMPRINT",EDGE,{"derivedFrom":subQ1}),1.0]])]});}
            var Q37;
            {var subQ1=sQuery(id+"F0.wireOp",EDGE,"E6.19.0");Q37=makeQuery(id+"F0.imprint","IMPRINT",FACE,{"disambiguationData":[TD([[makeQuery(id+"F0.imprint","IMPRINT",EDGE,{"derivedFrom":subQ1}),1.0]])]});}
            var Q38;
            {var subQ1=sQuery(id+"F0.wireOp",EDGE,"E6.20.0");Q38=makeQuery(id+"F0.imprint","IMPRINT",FACE,{"disambiguationData":[TD([[makeQuery(id+"F0.imprint","IMPRINT",EDGE,{"derivedFrom":subQ1}),1.0]])]});}
            var Q39;
            {var subQ0=sQuery(id+"F0.wireOp",EDGE,"E6.21.0");Q39=makeQuery(id+"F0.imprint","IMPRINT",FACE,{"disambiguationData":[TD([[makeQuery(id+"F0.imprint","IMPRINT",EDGE,{"derivedFrom":subQ0}),1.0]])]});}
            var Q40;
            {var subQ0=sQuery(id+"F0.wireOp",EDGE,"E6.22.0");Q40=makeQuery(id+"F0.imprint","IMPRINT",FACE,{"disambiguationData":[TD([[makeQuery(id+"F0.imprint","IMPRINT",EDGE,{"derivedFrom":subQ0}),1.0]])]});}
            var Q41;
            {var subQ1=sQuery(id+"F0.wireOp",EDGE,"E6.23.0");Q41=makeQuery(id+"F0.imprint","IMPRINT",FACE,{"disambiguationData":[TD([[makeQuery(id+"F0.imprint","IMPRINT",EDGE,{"derivedFrom":subQ1}),1.0]])]});}
            var Q42;
            {var subQ0=sQuery(id+"F0.wireOp",EDGE,"E6.24.0");Q42=makeQuery(id+"F0.imprint","IMPRINT",FACE,{"disambiguationData":[TD([[makeQuery(id+"F0.imprint","IMPRINT",EDGE,{"derivedFrom":subQ0}),1.0]])]});}
            extrude(context, id + "F1", {"entities" : qUnion([Q0, Q1, Q2, Q3, Q4, Q5, Q6, Q7, Q8, Q9, Q10, Q11, Q12, Q13, Q14, Q15, Q16, Q17, Q18, Q19, Q20, Q21, Q22, Q23, Q24, Q25, Q26, Q27, Q28, Q29, Q30, Q31, Q32, Q33, Q34, Q35, Q36, Q37, Q38, Q39, Q40, Q41, Q42]), "depth" : 25.4 * mm});
        }
        {
            var Q0;
            Q0=qCreatedBy(makeId("Front.planeOp"),FACE);
            var sketch = newSketch(context, id + "F2", { "sketchPlane" : qUnion([Q0])});
            skCircle(sketch, "E8", {"center": v(50.79, 41.85) * mm, "radius": 22.23 * mm});
            skCircle(sketch, "E9", {"center": v(50.79, 41.85) * mm, "radius": 12.07 * mm});
            skSolve(sketch);
        }
        {
            var Q0;
            Q0 = qSketchRegion(id + "F2", true);
            extrude(context, id + "F3", {"entities" : qUnion([Q0]), "depth" : 12.7 * mm});
        }
        {
            var Q0;
            Q0=qCreatedBy(makeId("Front.planeOp"),FACE);
            var sketch = newSketch(context, id + "F4", { "sketchPlane" : qUnion([Q0])});
            skCircle(sketch, "E10", {"center": v(-41.51, 46.83) * mm, "radius": 12.5 * mm});
            skSolve(sketch);
        }
        {
            var Q0;
            Q0 = qSketchRegion(id + "F4", true);
            extrude(context, id + "F5", {"entities" : qUnion([Q0]), "depth" : 22.8 * mm});
        }
        {
            var Q0;
            Q0=makeQuery(id+"F5.opExtrude","CAP_FACE",FACE,{"disambiguationData":[OSD([sQuery(id+"F4.wireOp",EDGE,"E10")])],"isStart":false});
            var sketch = newSketch(context, id + "F6", { "sketchPlane" : qUnion([Q0])});
            skCircle(sketch, "E11", {"center": v(-41.51, 46.83) * mm, "radius": 3 * mm});
            skSolve(sketch);
        }
        {
            var Q0;
            Q0 = qSketchRegion(id + "F6", true);
            extrude(context, id + "F7", {"entities" : qUnion([Q0]), "operationType" : NewBodyOperationType.ADD, "depth" : 4 * mm});
        }
        {
            var Q0;
            Q0=makeQuery(id+"F7.opExtrude","CAP_FACE",FACE,{"disambiguationData":[OSD([sQuery(id+"F6.wireOp",EDGE,"E11")])],"isStart":false});
            var sketch = newSketch(context, id + "F8", { "sketchPlane" : qUnion([Q0])});
            skCircle(sketch, "E12", {"center": v(-41.51, 46.83) * mm, "radius": 2 * mm});
            skSolve(sketch);
        }
        {
            var Q0;
            Q0 = qSketchRegion(id + "F8", true);
            extrude(context, id + "F9", {"entities" : qUnion([Q0]), "operationType" : NewBodyOperationType.ADD, "depth" : 12 * mm});
        }
        {
            var Q0;
            Q0=makeQuery(id+"F9.opExtrude","CAP_FACE",FACE,{"disambiguationData":[OSD([sQuery(id+"F8.wireOp",EDGE,"E12")])],"isStart":false});
            var sketch = newSketch(context, id + "F10", { "sketchPlane" : qUnion([Q0])});
            skLineSegment(sketch, "E13", {"start": v(-43.42, 47.44) * mm, "end": v(-39.6, 47.44) * mm});
            skArc(sketch, "E14", {"start": v(-39.6, 47.44) * mm, "mid": v(-41.51, 48.97) * mm, "end": v(-43.42, 47.44) * mm});
            skSolve(sketch);
        }
        {
            var Q0;
            Q0 = qSketchRegion(id + "F10", true);
            extrude(context, id + "F11", {"entities" : qUnion([Q0]), "operationType" : NewBodyOperationType.REMOVE, "oppositeDirection" : true, "depth" : 7.67 * mm});
        }
        {
            var Q0;
            Q0=makeQuery(id+"F5.opExtrude","CAP_FACE",FACE,{"disambiguationData":[OSD([sQuery(id+"F4.wireOp",EDGE,"E10")])],"isStart":false});
            var sketch = newSketch(context, id + "F12", { "sketchPlane" : qUnion([Q0])});
            skLineSegment(sketch, "E15", {"start": v(-41.51, 46.83) * mm, "end": v(-50.01, 46.83) * mm});
            skLineSegment(sketch, "E16", {"start": v(-41.51, 46.83) * mm, "end": v(-41.51, 51.03) * mm});
            skCircle(sketch, "E17", {"center": v(-50.01, 46.83) * mm, "radius": 1.5 * mm});
            skCircle(sketch, "E18.MirrorC", {"center": v(-33.01, 46.83) * mm, "radius": 1.5 * mm});
            skLineSegment(sketch, "E19.MirrorCS", {"start": v(-41.51, 46.83) * mm, "end": v(-33.01, 46.83) * mm});
            skSolve(sketch);
        }
        {
            var Q0;
            Q0 = qSketchRegion(id + "F12", true);
            extrude(context, id + "F13", {"entities" : qUnion([Q0]), "operationType" : NewBodyOperationType.REMOVE, "oppositeDirection" : true, "depth" : 12.7 * mm});
        }
        {
            var Q0;
            Q0=makeQuery(id+"F5.opExtrude","CAP_FACE",FACE,{"disambiguationData":[OSD([sQuery(id+"F4.wireOp",EDGE,"E10")])],"isStart":true});
            var sketch = newSketch(context, id + "F14", { "sketchPlane" : qUnion([Q0])});
            skCircle(sketch, "E20", {"center": v(41.51, 46.83) * mm, "radius": 2.64 * mm});
            skSolve(sketch);
        }
        {
            var Q0;
            Q0 = qSketchRegion(id + "F14", true);
            extrude(context, id + "F15", {"entities" : qUnion([Q0]), "operationType" : NewBodyOperationType.REMOVE, "oppositeDirection" : true, "depth" : 2.54 * mm});
        }
        {
            var Q0;
            Q0=qCreatedBy(makeId("Front.planeOp"),FACE);
            var sketch = newSketch(context, id + "F16", { "sketchPlane" : qUnion([Q0])});
            skCircle(sketch, "E21", {"center": v(-49.03, -41.2) * mm, "radius": 14.33 * mm});
            skSolve(sketch);
        }
        {
            var Q0;
            Q0 = qSketchRegion(id + "F16", true);
            extrude(context, id + "F17", {"entities" : qUnion([Q0]), "depth" : 4.3 * mm});
        }
        {
            var Q0;
            Q0=makeQuery(id+"F17.opExtrude","CAP_FACE",FACE,{"disambiguationData":[OSD([sQuery(id+"F16.wireOp",EDGE,"E21")])],"isStart":false});
            var sketch = newSketch(context, id + "F18", { "sketchPlane" : qUnion([Q0])});
            skCircle(sketch, "E22", {"center": v(-49.03, -41.2) * mm, "radius": 17.48 * mm});
            skSolve(sketch);
        }
        {
            var Q0;
            Q0 = qSketchRegion(id + "F18", true);
            extrude(context, id + "F19", {"entities" : qUnion([Q0]), "operationType" : NewBodyOperationType.ADD, "depth" : 1.5 * mm});
        }
        {
            var Q0;
            Q0=makeQuery(id+"F17.opExtrude","CAP_FACE",FACE,{"disambiguationData":[OSD([sQuery(id+"F16.wireOp",EDGE,"E21")])],"isStart":true});
            var sketch = newSketch(context, id + "F20", { "sketchPlane" : qUnion([Q0])});
            skCircle(sketch, "E23", {"center": v(49.03, -41.2) * mm, "radius": 17.47 * mm});
            skSolve(sketch);
        }
        {
            var Q0;
            Q0 = qSketchRegion(id + "F20", true);
            extrude(context, id + "F21", {"entities" : qUnion([Q0]), "operationType" : NewBodyOperationType.ADD, "depth" : 1.5 * mm});
        }
        {
            var Q0;
            Q0=makeQuery(id+"F21.opExtrude","CAP_FACE",FACE,{"disambiguationData":[OSD([sQuery(id+"F20.wireOp",EDGE,"E23")])],"isStart":false});
            var sketch = newSketch(context, id + "F22", { "sketchPlane" : qUnion([Q0])});
            skCircle(sketch, "E24", {"center": v(49.03, -41.2) * mm, "radius": 6.35 * mm});
            skSolve(sketch);
        }
        {
            var Q0;
            Q0 = qSketchRegion(id + "F22", true);
            extrude(context, id + "F23", {"entities" : qUnion([Q0]), "operationType" : NewBodyOperationType.ADD, "depth" : 4.6 * mm});
        }
        {
            var Q0;
            Q0=makeQuery(id+"F23.opExtrude","CAP_FACE",FACE,{"disambiguationData":[OSD([sQuery(id+"F22.wireOp",EDGE,"E24")])],"isStart":false});
            var sketch = newSketch(context, id + "F24", { "sketchPlane" : qUnion([Q0])});
            skCircle(sketch, "E25", {"center": v(49.03, -41.2) * mm, "radius": 2 * mm});
            skSolve(sketch);
        }
        {
            var Q0;
            Q0 = qSketchRegion(id + "F24", true);
            extrude(context, id + "F25", {"entities" : qUnion([Q0]), "operationType" : NewBodyOperationType.REMOVE, "endBound" : BoundingType.THROUGH_ALL, "oppositeDirection" : true, "depth" : 25.4 * mm});
        }
        {
            var Q0;
            Q0=qCreatedBy(makeId("Front.planeOp"),FACE);
            var sketch = newSketch(context, id + "F26", { "sketchPlane" : qUnion([Q0])});
            skLineSegment(sketch, "E26.bottom", {"start": v(-18.8, 10.53) * mm, "end": v(103.38, 10.53) * mm});
            skLineSegment(sketch, "E26.top", {"start": v(-18.8, -40.27) * mm, "end": v(108.2, -40.27) * mm});
            skLineSegment(sketch, "E26.left", {"start": v(-31.5, -2.17) * mm, "end": v(-31.5, -27.57) * mm});
            skLineSegment(sketch, "E27.bottom", {"start": v(108.2, -40.27) * mm, "end": v(157.2, -40.27) * mm});
            skLineSegment(sketch, "E27.top", {"start": v(108.2, -40.27) * mm, "end": v(157.2, -40.27) * mm});
            skLineSegment(sketch, "E27.left", {"start": v(108.2, -40.27) * mm, "end": v(108.2, -40.27) * mm});
            skLineSegment(sketch, "E27.right", {"start": v(157.2, -40.27) * mm, "end": v(157.2, -40.27) * mm});
            skLineSegment(sketch, "E28", {"start": v(157.2, -40.27) * mm, "end": v(112.07, -12.88) * mm});
            skPoint(sketch, "E29.visualSharp", {"position": v(-31.5, 10.53) * mm});
            skArc(sketch, "E29.filletArc", {"start": v(-18.8, 10.53) * mm, "mid": v(-27.77, 6.8) * mm, "end": v(-31.5, -2.17) * mm});
            skPoint(sketch, "E30.visualSharp", {"position": v(-31.5, -40.27) * mm});
            skArc(sketch, "E30.filletArc", {"start": v(-31.5, -27.57) * mm, "mid": v(-27.77, -36.55) * mm, "end": v(-18.8, -40.27) * mm});
            skLineSegment(sketch, "E31", {"start": v(112.07, -12.88) * mm, "end": v(103.38, 10.53) * mm});
            skArc(sketch, "E32", {"start": v(103.38, 10.53) * mm, "mid": v(78.48, 27.84) * mm, "end": v(53.59, 10.53) * mm});
            skSolve(sketch);
        }
        {
            var Q0;
            Q0 = qSketchRegion(id + "F26", true);
            extrude(context, id + "F27", {"entities" : qUnion([Q0]), "depth" : 12.7 * mm});
        }
        {
            var Q0;
            Q0=makeQuery(id+"F27.opExtrude","CAP_FACE",FACE,{"disambiguationData":[OSD([sQuery(id+"F26.wireOp",EDGE,"E26.bottom"),sQuery(id+"F26.wireOp",EDGE,"E26.top"),sQuery(id+"F26.wireOp",EDGE,"E26.left"),sQuery(id+"F26.wireOp",EDGE,"E26.right"),sQuery(id+"F26.wireOp",EDGE,"E27.top"),sQuery(id+"F26.wireOp",EDGE,"E28")])],"isStart":false});
            var sketch = newSketch(context, id + "F28", { "sketchPlane" : qUnion([Q0])});
            skCircle(sketch, "E33", {"center": v(-12.57, -14.87) * mm, "radius": 12.14 * mm});
            skPoint(sketch, "E33.centerSnap0", {"position": v(-31.5, -14.87) * mm});
            skCircle(sketch, "E34", {"center": v(84.81, -14.87) * mm, "radius": 3.18 * mm});
            skCircle(sketch, "E35", {"center": v(83.6, 10.53) * mm, "radius": 4.76 * mm});
            skSolve(sketch);
        }
        {
            var Q0;
            Q0 = qSketchRegion(id + "F28", true);
            extrude(context, id + "F29", {"entities" : qUnion([Q0]), "operationType" : NewBodyOperationType.REMOVE, "endBound" : BoundingType.THROUGH_ALL, "oppositeDirection" : true, "depth" : 25.4 * mm});
        }
        {
            var Q0;
            Q0=qCreatedBy(makeId("Right.planeOp"),FACE);
            var sketch = newSketch(context, id + "F30", { "sketchPlane" : qUnion([Q0])});
            skArc(sketch, "E36", {"start": v(18.97, -16.58) * mm, "mid": v(50.98, -56.5) * mm, "end": v(58.63, -5.9) * mm});
            skLineSegment(sketch, "E37", {"start": v(18.97, -16.58) * mm, "end": v(40.75, 25.07) * mm});
            skLineSegment(sketch, "E38", {"start": v(46.1, 30.43) * mm, "end": v(67.17, 41.49) * mm});
            skLineSegment(sketch, "E39", {"start": v(58.63, -5.9) * mm, "end": v(56.65, 11.2) * mm});
            skLineSegment(sketch, "E40", {"start": v(57.48, 17.4) * mm, "end": v(67.17, 41.49) * mm});
            skPoint(sketch, "E41.visualSharp", {"position": v(56.28, 14.4) * mm});
            skArc(sketch, "E41.filletArc", {"start": v(57.48, 17.4) * mm, "mid": v(56.68, 14.35) * mm, "end": v(56.65, 11.2) * mm});
            skPoint(sketch, "E42.visualSharp", {"position": v(42.59, 28.6) * mm});
            skArc(sketch, "E42.filletArc", {"start": v(46.1, 30.43) * mm, "mid": v(43.02, 28.16) * mm, "end": v(40.75, 25.07) * mm});
            skSolve(sketch);
        }
        {
            var Q0;
            Q0 = qSketchRegion(id + "F30", true);
            extrude(context, id + "F31", {"entities" : qUnion([Q0]), "depth" : 9.52 * mm});
        }
    });
